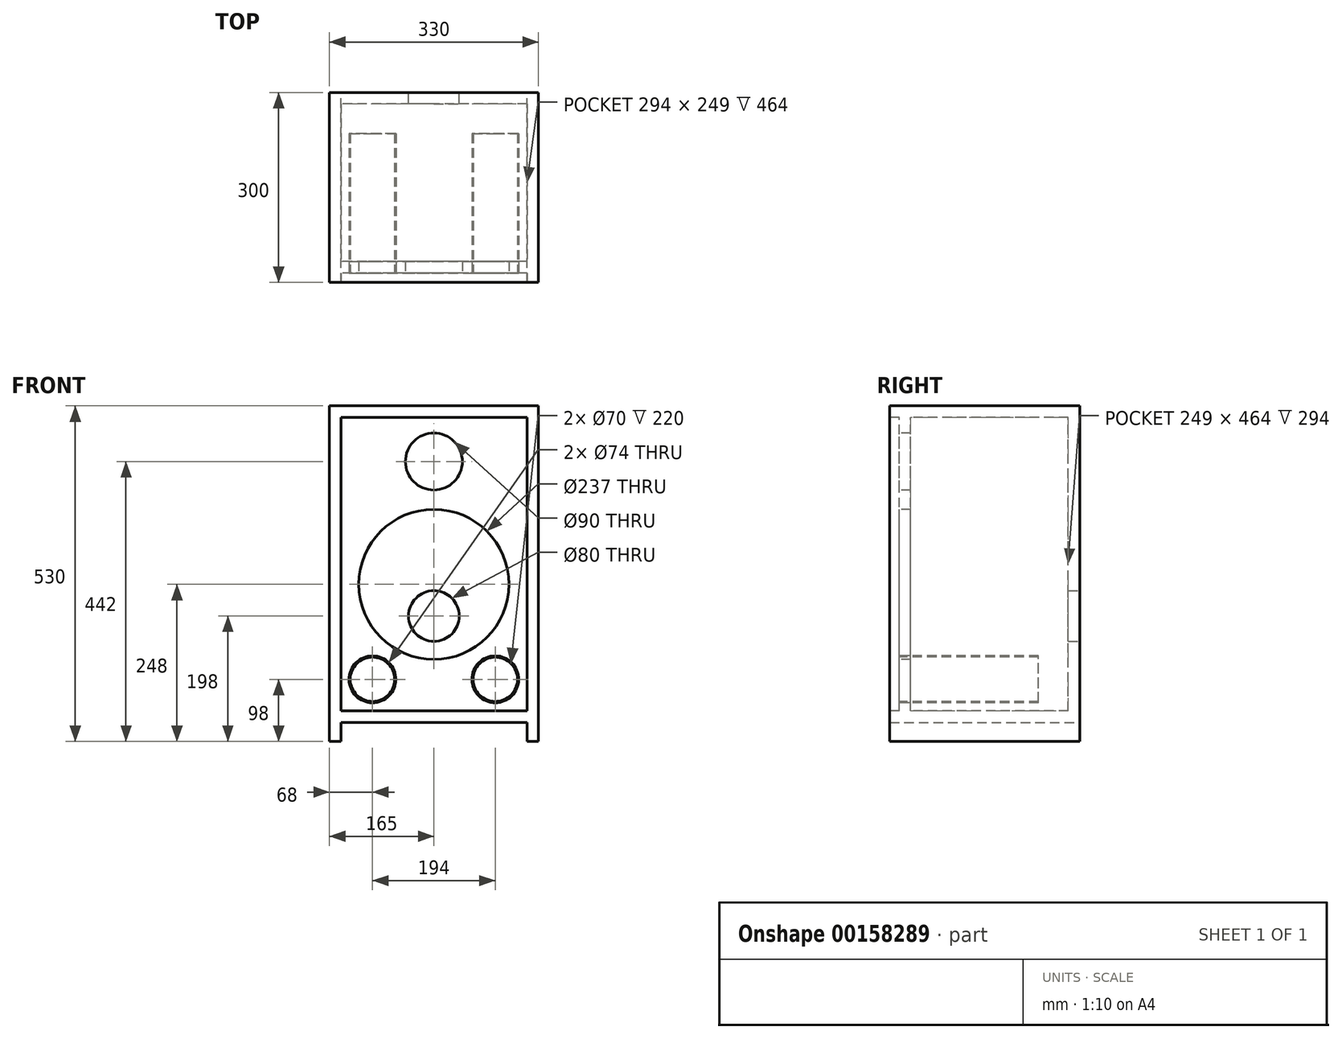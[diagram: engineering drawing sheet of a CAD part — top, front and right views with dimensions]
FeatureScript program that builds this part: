
annotation { "Feature Type Name" : "Feature", "Feature Type Description" : "" }
export const myFeature = defineFeature(function(context is Context, id is Id, definition is map)
    precondition{}
    {
        {
            var Q0;
            Q0=qCreatedBy(makeId("Front.planeOp"),FACE);
            var sketch = newSketch(context, id + "F0", { "sketchPlane" : qUnion([Q0])});
            skLineSegment(sketch, "E0.bottom", {"start": v(-165, -265) * mm, "end": v(-147, -265) * mm});
            skLineSegment(sketch, "E0.top", {"start": v(-165, 265) * mm, "end": v(165, 265) * mm});
            skLineSegment(sketch, "E0.left", {"start": v(-165, -265) * mm, "end": v(-165, 265) * mm});
            skLineSegment(sketch, "E0.right", {"start": v(165, -265) * mm, "end": v(165, 265) * mm});
            skPoint(sketch, "E0.middle", {"position": v(0, 0) * mm});
            skLineSegment(sketch, "E1", {"start": v(-147, -265) * mm, "end": v(-147, -235) * mm});
            skLineSegment(sketch, "E2", {"start": v(-147, -235) * mm, "end": v(147, -235) * mm});
            skLineSegment(sketch, "E3", {"start": v(147, -235) * mm, "end": v(147, -265) * mm});
            skLineSegment(sketch, "E4.trimOffspring", {"start": v(147, -265) * mm, "end": v(165, -265) * mm});
            skSolve(sketch);
        }
        {
            var Q0;
            Q0=makeQuery(id+"F0.imprint","IMPRINT",FACE,{"disambiguationData":[TD([[makeQuery(id+"F0.imprint","IMPRINT",EDGE,{"derivedFrom":sQuery(id+"F0.wireOp",EDGE,"E0.bottom")}),1.0]])]});
            extrude(context, id + "F1", {"entities" : qUnion([Q0]), "endBound" : BoundingType.SYMMETRIC, "depth" : 300 * mm});
        }
        {
            var Q0;
            Q0=makeQuery(id+"F1.opExtrude","CAP_FACE",FACE,{"disambiguationData":[OSD([sQuery(id+"F0.wireOp",EDGE,"E0.bottom"),sQuery(id+"F0.wireOp",EDGE,"E0.top"),sQuery(id+"F0.wireOp",EDGE,"E0.left"),sQuery(id+"F0.wireOp",EDGE,"E0.right"),sQuery(id+"F0.wireOp",EDGE,"E1"),sQuery(id+"F0.wireOp",EDGE,"E2"),sQuery(id+"F0.wireOp",EDGE,"E3"),sQuery(id+"F0.wireOp",EDGE,"E4.trimOffspring")])],"isStart":false});
            var sketch = newSketch(context, id + "F2", { "sketchPlane" : qUnion([Q0])});
            skLineSegment(sketch, "E5.bottom", {"start": v(147, -217) * mm, "end": v(-147, -217) * mm});
            skLineSegment(sketch, "E5.top", {"start": v(147, 247) * mm, "end": v(-147, 247) * mm});
            skLineSegment(sketch, "E5.left", {"start": v(147, -217) * mm, "end": v(147, 247) * mm});
            skLineSegment(sketch, "E5.right", {"start": v(-147, -217) * mm, "end": v(-147, 247) * mm});
            skPoint(sketch, "E5.middle", {"position": v(0, 15) * mm});
            skSolve(sketch);
        }
        {
            var Q0;
            Q0 = qSketchRegion(id + "F2", true);
            extrude(context, id + "F3", {"entities" : qUnion([Q0]), "operationType" : NewBodyOperationType.REMOVE, "oppositeDirection" : true, "depth" : 282 * mm});
        }
        {
            var Q0;
            Q0=makeQuery(id+"F1.opExtrude","CAP_FACE",FACE,{"disambiguationData":[OSD([sQuery(id+"F0.wireOp",EDGE,"E0.bottom"),sQuery(id+"F0.wireOp",EDGE,"E0.top"),sQuery(id+"F0.wireOp",EDGE,"E0.left"),sQuery(id+"F0.wireOp",EDGE,"E0.right"),sQuery(id+"F0.wireOp",EDGE,"E1"),sQuery(id+"F0.wireOp",EDGE,"E2"),sQuery(id+"F0.wireOp",EDGE,"E3"),sQuery(id+"F0.wireOp",EDGE,"E4.trimOffspring")])],"isStart":false});
            var sketch = newSketch(context, id + "F4", { "sketchPlane" : qUnion([Q0])});
            skLineSegment(sketch, "E6.bottom", {"start": v(-147, 247) * mm, "end": v(147, 247) * mm});
            skLineSegment(sketch, "E6.top", {"start": v(-147, -217) * mm, "end": v(147, -217) * mm});
            skLineSegment(sketch, "E6.left", {"start": v(-147, 247) * mm, "end": v(-147, -217) * mm});
            skLineSegment(sketch, "E6.right", {"start": v(147, 247) * mm, "end": v(147, -217) * mm});
            skCircle(sketch, "E7", {"center": v(0, 177) * mm, "radius": 45 * mm});
            skCircle(sketch, "E8", {"center": v(-97, -167) * mm, "radius": 37 * mm});
            skCircle(sketch, "E9", {"center": v(97, -167) * mm, "radius": 37 * mm});
            skCircle(sketch, "E10", {"center": v(0, -17) * mm, "radius": 118.5 * mm});
            skLineSegment(sketch, "E11", {"start": v(0, -217) * mm, "end": v(0, 247) * mm, "construction": true});
            skSolve(sketch);
        }
        {
            var Q0;
            Q0 = qSketchRegion(id + "F4", true);
            extrude(context, id + "F5", {"entities" : qUnion([Q0]), "operationType" : NewBodyOperationType.ADD, "oppositeDirection" : true, "depth" : 33 * mm});
        }
        {
            var Q0;
            Q0 = qSketchRegion(id + "F4", true);
            extrude(context, id + "F6", {"entities" : qUnion([Q0]), "operationType" : NewBodyOperationType.REMOVE, "oppositeDirection" : true, "depth" : 15 * mm});
        }
        {
            var Q0;
            Q0=makeQuery(id+"F1.opExtrude","CAP_FACE",FACE,{"disambiguationData":[OSD([sQuery(id+"F0.wireOp",EDGE,"E0.bottom"),sQuery(id+"F0.wireOp",EDGE,"E0.top"),sQuery(id+"F0.wireOp",EDGE,"E0.left"),sQuery(id+"F0.wireOp",EDGE,"E0.right"),sQuery(id+"F0.wireOp",EDGE,"E1"),sQuery(id+"F0.wireOp",EDGE,"E2"),sQuery(id+"F0.wireOp",EDGE,"E3"),sQuery(id+"F0.wireOp",EDGE,"E4.trimOffspring")])],"isStart":true});
            var sketch = newSketch(context, id + "F7", { "sketchPlane" : qUnion([Q0])});
            skCircle(sketch, "E12", {"center": v(0, -67) * mm, "radius": 40 * mm});
            skSolve(sketch);
        }
        {
            var Q0;
            Q0 = qSketchRegion(id + "F7", true);
            extrude(context, id + "F8", {"entities" : qUnion([Q0]), "operationType" : NewBodyOperationType.REMOVE, "endBound" : BoundingType.UP_TO_NEXT, "oppositeDirection" : true, "depth" : 25 * mm});
        }
        {
            var Q0;
            Q0=makeQuery(id+"F6.boolean.opBoolean","COPY",FACE,{"derivedFrom":makeQuery(id+"F6.opExtrude","CAP_FACE",FACE,{"disambiguationData":[OSD([sQuery(id+"F4.wireOp",EDGE,"E6.bottom"),sQuery(id+"F4.wireOp",EDGE,"E6.top"),sQuery(id+"F4.wireOp",EDGE,"E6.left"),sQuery(id+"F4.wireOp",EDGE,"E6.right"),sQuery(id+"F4.wireOp",EDGE,"E7"),sQuery(id+"F4.wireOp",EDGE,"E8"),sQuery(id+"F4.wireOp",EDGE,"E9"),sQuery(id+"F4.wireOp",EDGE,"E10")])],"isStart":false})});
            var sketch = newSketch(context, id + "F9", { "sketchPlane" : qUnion([Q0])});
            skCircle(sketch, "E13", {"center": v(-97, -167) * mm, "radius": 37 * mm});
            skCircle(sketch, "E14", {"center": v(97, -167) * mm, "radius": 37 * mm});
            skCircle(sketch, "E15", {"center": v(97, -167) * mm, "radius": 35 * mm});
            skCircle(sketch, "E16", {"center": v(-97, -167) * mm, "radius": 35 * mm});
            skSolve(sketch);
        }
        {
            var Q0;
            Q0 = qSketchRegion(id + "F9", true);
            extrude(context, id + "F10", {"entities" : qUnion([Q0]), "oppositeDirection" : true, "depth" : 220 * mm});
        }
    });
